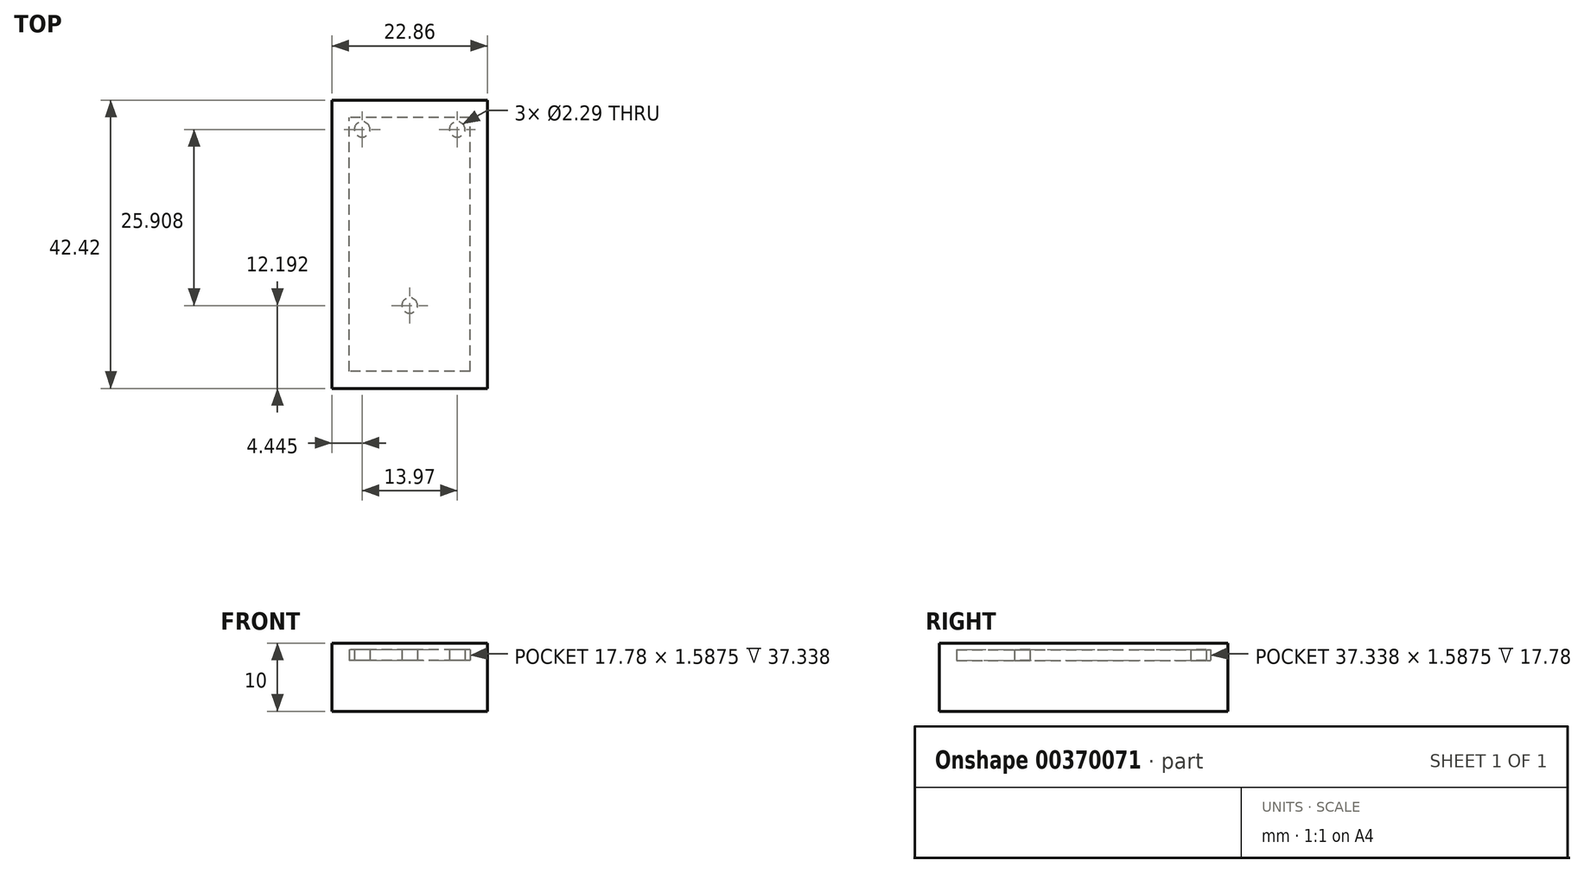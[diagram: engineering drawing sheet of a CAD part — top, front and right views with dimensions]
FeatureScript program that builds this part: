
annotation { "Feature Type Name" : "Feature", "Feature Type Description" : "" }
export const myFeature = defineFeature(function(context is Context, id is Id, definition is map)
    precondition{}
    {
        {
            var Q0;
            Q0=qCreatedBy(makeId("Top.planeOp"),FACE);
            var sketch = newSketch(context, id + "F0", { "sketchPlane" : qUnion([Q0])});
            skLineSegment(sketch, "E0.bottom", {"start": v(0, 0) * mm, "end": v(-17.78, 0) * mm});
            skLineSegment(sketch, "E0.top", {"start": v(0, 37.34) * mm, "end": v(-17.78, 37.34) * mm});
            skLineSegment(sketch, "E0.left", {"start": v(0, 0) * mm, "end": v(0, 37.34) * mm});
            skLineSegment(sketch, "E0.right", {"start": v(-17.78, 0) * mm, "end": v(-17.78, 37.34) * mm});
            skCircle(sketch, "E1", {"center": v(-15.88, 35.56) * mm, "radius": 1.14 * mm});
            skCircle(sketch, "E2", {"center": v(-1.9, 35.56) * mm, "radius": 1.14 * mm});
            skCircle(sketch, "E3", {"center": v(-8.9, 9.65) * mm, "radius": 1.14 * mm});
            skSolve(sketch);
        }
        {
            var Q0;
            Q0=makeQuery(id+"F0.imprint","IMPRINT",FACE,{"disambiguationData":[TD([[makeQuery(id+"F0.imprint","IMPRINT",EDGE,{"derivedFrom":sQuery(id+"F0.wireOp",EDGE,"E0.bottom")}),-1.0]])]});
            extrude(context, id + "F1", {"entities" : qUnion([Q0]), "depth" : 1.59 * mm});
        }
        {
            var Q0;
            Q0=makeQuery(id+"F1.opExtrude","CAP_FACE",FACE,{"disambiguationData":[OSD([sQuery(id+"F0.wireOp",EDGE,"E0.bottom"),sQuery(id+"F0.wireOp",EDGE,"E0.top"),sQuery(id+"F0.wireOp",EDGE,"E0.left"),sQuery(id+"F0.wireOp",EDGE,"E0.right"),sQuery(id+"F0.wireOp",EDGE,"E1"),sQuery(id+"F0.wireOp",EDGE,"E2"),sQuery(id+"F0.wireOp",EDGE,"E3")])],"isStart":true});
            cPlane(context, id + "F2", {"entities" : qUnion([Q0]), "cplaneType" : CPlaneType.OFFSET, "offset" : 2.54 * mm, "oppositeDirection" : true, "width" : 152.4 * mm, "height" : 152.4 * mm});
        }
        {
            var Q0;
            Q0=qCreatedBy(id+"F2.planeOp",FACE);
            var sketch = newSketch(context, id + "F3", { "sketchPlane" : qUnion([Q0])});
            skLineSegment(sketch, "E4.0", {"start": v(0, -37.34) * mm, "end": v(-17.78, -37.34) * mm});
            skLineSegment(sketch, "E5.0", {"start": v(-17.78, 0) * mm, "end": v(-17.78, -37.34) * mm});
            skLineSegment(sketch, "E6.0", {"start": v(0, 0) * mm, "end": v(0, -37.34) * mm});
            skLineSegment(sketch, "E7.0", {"start": v(0, 0) * mm, "end": v(-17.78, 0) * mm});
            skLineSegment(sketch, "E8.0", {"start": v(2.54, 2.54) * mm, "end": v(2.54, -39.88) * mm});
            skLineSegment(sketch, "E8.1", {"start": v(2.54, 2.54) * mm, "end": v(-20.32, 2.54) * mm});
            skLineSegment(sketch, "E8.2", {"start": v(-20.32, 2.54) * mm, "end": v(-20.32, -39.88) * mm});
            skLineSegment(sketch, "E8.3", {"start": v(2.54, -39.88) * mm, "end": v(-20.32, -39.88) * mm});
            skSolve(sketch);
        }
        {
            var Q0;
            Q0=makeQuery(id+"F3.imprint","IMPRINT",FACE,{"disambiguationData":[TD([[makeQuery(id+"F3.imprint","IMPRINT",EDGE,{"derivedFrom":sQuery(id+"F3.wireOp",EDGE,"E4.0")}),-1.0]])]});
            var Q1;
            Q1=makeQuery(id+"F3.imprint","IMPRINT",FACE,{"disambiguationData":[TD([[makeQuery(id+"F3.imprint","IMPRINT",EDGE,{"derivedFrom":sQuery(id+"F3.wireOp",EDGE,"db449c86-7805-4fbe-af88-7e8c0a7d5b73.0")}),-1.0]])]});
            var Q2;
            Q2=makeQuery(id+"F3.imprint","IMPRINT",FACE,{"disambiguationData":[TD([[makeQuery(id+"F3.imprint","IMPRINT",EDGE,{"derivedFrom":sQuery(id+"F3.wireOp",EDGE,"724c7534-67da-4bd6-9467-e42802b80d22.0")}),1.0]])]});
            var Q3;
            Q3=makeQuery(id+"F3.imprint","IMPRINT",FACE,{"disambiguationData":[TD([[makeQuery(id+"F3.imprint","IMPRINT",EDGE,{"derivedFrom":sQuery(id+"F3.wireOp",EDGE,"db449c86-7805-4fbe-af88-7e8c0a7d5b73.0")}),1.0]])]});
            var Q4;
            Q4=makeQuery(id+"F3.imprint","IMPRINT",FACE,{"disambiguationData":[TD([[makeQuery(id+"F3.imprint","IMPRINT",EDGE,{"derivedFrom":sQuery(id+"F3.wireOp",EDGE,"724c7534-67da-4bd6-9467-e42802b80d22.0")}),-1.0]])]});
            var Q5;
            Q5=makeQuery(id+"F3.imprint","IMPRINT",FACE,{"disambiguationData":[TD([[makeQuery(id+"F3.imprint","IMPRINT",EDGE,{"derivedFrom":sQuery(id+"F3.wireOp",EDGE,"E4.0")}),1.0]])]});
            var Q6;
            Q6=makeQuery(id+"F3.imprint","IMPRINT",FACE,{"disambiguationData":[TD([[makeQuery(id+"F3.imprint","IMPRINT",EDGE,{"derivedFrom":sQuery(id+"F3.wireOp",EDGE,"f6b61f14-276f-4158-92af-6dfaea2c19e1.0")}),-1.0]])]});
            extrude(context, id + "F4", {"entities" : qUnion([Q0, Q1, Q2, Q3, Q4, Q5, Q6]), "depth" : 10 * mm});
        }
        {
            var Q0;
            Q0=makeQuery(id+"F1.opExtrude","SWEPT_BODY",BODY,{"disambiguationData":[OSD([sQuery(id+"F0.wireOp",EDGE,"E0.bottom"),sQuery(id+"F0.wireOp",EDGE,"E0.top"),sQuery(id+"F0.wireOp",EDGE,"E0.left"),sQuery(id+"F0.wireOp",EDGE,"E0.right"),sQuery(id+"F0.wireOp",EDGE,"E1"),sQuery(id+"F0.wireOp",EDGE,"E2"),sQuery(id+"F0.wireOp",EDGE,"E3")])]});
            var Q1;
            Q1=makeQuery(id+"F4.opExtrude","SWEPT_BODY",BODY,{"disambiguationData":[OSD([sQuery(id+"F3.wireOp",EDGE,"E8.0"),sQuery(id+"F3.wireOp",EDGE,"E8.1"),sQuery(id+"F3.wireOp",EDGE,"E8.2"),sQuery(id+"F3.wireOp",EDGE,"E8.3")])]});
            booleanBodies(context, id + "F5", {"operationType" : BooleanOperationType.SUBTRACTION, "tools" : qUnion([Q0]), "targets" : qUnion([Q1]), "offsetAll" : true, "keepTools" : true});
        }
    });
